# Revit family: Haworth_ASeries_Credenza_1HighStorageEnd
name_source: partatom
category: Furniture Systems
revit_build: Autodesk Revit 2018 (Build: 20170223_1515(x64)
units: mm (PartAtom-declared; Revit-internal decimal feet)

## family parameters
Always vertical = Yes
Cut with Voids When Loaded = No
OmniClass Number = 23.40.70.14.64.21
OmniClass Title = Systems Furniture
Part Type = Normal
Room Calculation Point = No
Round Connector Dimension = Use Diameter
Shared = No
Work Plane-Based = No

## types (9) — shared parameters
Actual Depth = 18"
Actual Height = 21 1/4"
Assembly Code = E2020200
Base Height = 2 1/2"
Classic Pull = Yes
Crescent Pull = No
Custom Size = No
Description = Haworth - ASeries Credenza - 1-High - Storage End
Door Height = 18"
Door Offset = 2"
Drawer Height = 6"
Drawer Height Bottom = 11 15/16"
Ellipse Pull = No
End Shelf Height = 11 1/2"
Front Finish = Haworth _ Laminate _ Linen H-WL
Full Back = Yes
J Pull = No
Linear Pull = No
Manufacturer = Haworth
Max. Height = 21 1/4"
Max. Width = 72"
Metal Offset = 1/16"
Min. Height = 21 1/4"
Min. Width = 48"
Min/Max Widths = 48-72 in.
Model = GCLS
Pull Finish = Haworth _ Metal _ Brushed Aluminum
Radius Pull = No
Revision Number = 2
Shelf Finish = Haworth _ Laminate _ Linen H-WL
Size = Verify Final Dim. w/ Haworth
Standard Base = Yes
Storage Back = No
Sustainability Info = https://www.haworth.com
Taper Pull = No
Toe Kick Base = No
Toe Kick Height = 1 3/4"
Top Finish = Haworth _ Laminate _ Linen H-WL
URL = www.haworth.com
URL - Product = https://www.haworth.com
Warranty = http://www.haworth.com

## per-type parameters (varying)
- 72w - 36w Drawers: Actual Storage Width=36"; Actual Width=72"; Door Center=19 3/8"; Door Width=17 15/16"; Drawers=Yes; Hinged Doors=No; Max. Storage Width=42"; Middle Shelf Height=11 1/2"; Min. Storage Width=30"; Open=No; Panel Center Offset=18 1/8"; Right Panel=Yes; Right Shelf Length=23 7/8"; Shelf Offset=3/4"; Standard Size Doors 48=No; Standard Size Doors 60=No; Standard Size Doors 72=No; Standard Size Lat 48=No; Standard Size Lat 60=No; Standard Size Lat 72=Yes; Standard Size Open 48=No; Standard Size Open 60=No; Standard Size Open 72=No; Storage Width=36"; Width=72"
- 72w - 36w Doors: Actual Storage Width=36"; Actual Width=72"; Door Center=19 3/8"; Door Width=17 15/16"; Drawers=No; Hinged Doors=Yes; Max. Storage Width=42"; Middle Shelf Height=16 3/4"; Min. Storage Width=30"; Open=No; Panel Center Offset=18 1/8"; Right Panel=Yes; Right Shelf Length=23 7/8"; Shelf Offset=3/4"; Standard Size Doors 48=No; Standard Size Doors 60=No; Standard Size Doors 72=Yes; Standard Size Lat 48=No; Standard Size Lat 60=No; Standard Size Lat 72=No; Standard Size Open 48=No; Standard Size Open 60=No; Standard Size Open 72=No; Storage Width=36"; Width=72"
- 72w - 36w Open: Actual Storage Width=36"; Actual Width=72"; Door Center=19 3/8"; Door Width=17 15/16"; Drawers=No; Hinged Doors=No; Max. Storage Width=42"; Middle Shelf Height=11 1/2"; Min. Storage Width=30"; Open=Yes; Panel Center Offset=18 1/8"; Right Panel=Yes; Right Shelf Length=23 7/8"; Shelf Offset=3/4"; Standard Size Doors 48=No; Standard Size Doors 60=No; Standard Size Doors 72=No; Standard Size Lat 48=No; Standard Size Lat 60=No; Standard Size Lat 72=No; Standard Size Open 48=No; Standard Size Open 60=No; Standard Size Open 72=Yes; Storage Width=36"; Width=72"
- 60w - 30w Drawers: Actual Storage Width=30"; Actual Width=60"; Door Center=16 3/8"; Door Width=14 15/16"; Drawers=Yes; Hinged Doors=No; Max. Storage Width=42"; Middle Shelf Height=11 1/2"; Min. Storage Width=30"; Open=No; Panel Center Offset=15 1/8"; Right Panel=Yes; Right Shelf Length=17 7/8"; Shelf Offset=3/4"; Standard Size Doors 48=No; Standard Size Doors 60=No; Standard Size Doors 72=No; Standard Size Lat 48=No; Standard Size Lat 60=Yes; Standard Size Lat 72=No; Standard Size Open 48=No; Standard Size Open 60=No; Standard Size Open 72=No; Storage Width=30"; Width=60"
- 60w - 30w Doors: Actual Storage Width=30"; Actual Width=60"; Door Center=16 3/8"; Door Width=14 15/16"; Drawers=No; Hinged Doors=Yes; Max. Storage Width=42"; Middle Shelf Height=16 3/4"; Min. Storage Width=30"; Open=No; Panel Center Offset=15 1/8"; Right Panel=Yes; Right Shelf Length=17 7/8"; Shelf Offset=3/4"; Standard Size Doors 48=No; Standard Size Doors 60=Yes; Standard Size Doors 72=No; Standard Size Lat 48=No; Standard Size Lat 60=No; Standard Size Lat 72=No; Standard Size Open 48=No; Standard Size Open 60=No; Standard Size Open 72=No; Storage Width=30"; Width=60"
- 60w - 30w Open: Actual Storage Width=30"; Actual Width=60"; Door Center=16 3/8"; Door Width=14 15/16"; Drawers=No; Hinged Doors=No; Max. Storage Width=42"; Middle Shelf Height=11 1/2"; Min. Storage Width=30"; Open=Yes; Panel Center Offset=15 1/8"; Right Panel=Yes; Right Shelf Length=17 7/8"; Shelf Offset=3/4"; Standard Size Doors 48=No; Standard Size Doors 60=No; Standard Size Doors 72=No; Standard Size Lat 48=No; Standard Size Lat 60=No; Standard Size Lat 72=No; Standard Size Open 48=No; Standard Size Open 60=Yes; Standard Size Open 72=No; Storage Width=30"; Width=60"
- 48w - 24w Drawers: Actual Storage Width=24"; Actual Width=48"; Door Center=13 3/8"; Door Width=11 15/16"; Drawers=Yes; Hinged Doors=No; Max. Storage Width=30"; Middle Shelf Height=11 1/2"; Min. Storage Width=24"; Open=No; Panel Center Offset=12 1/8"; Right Panel=No; Right Shelf Length=11 7/8"; Shelf Offset=1/16"; Standard Size Doors 48=No; Standard Size Doors 60=No; Standard Size Doors 72=No; Standard Size Lat 48=Yes; Standard Size Lat 60=No; Standard Size Lat 72=No; Standard Size Open 48=No; Standard Size Open 60=No; Standard Size Open 72=No; Storage Width=24"; Width=48"
- 48w - 24w Doors: Actual Storage Width=24"; Actual Width=48"; Door Center=13 3/8"; Door Width=11 15/16"; Drawers=No; Hinged Doors=Yes; Max. Storage Width=30"; Middle Shelf Height=16 3/4"; Min. Storage Width=24"; Open=No; Panel Center Offset=12 1/8"; Right Panel=No; Right Shelf Length=11 7/8"; Shelf Offset=1/16"; Standard Size Doors 48=Yes; Standard Size Doors 60=No; Standard Size Doors 72=No; Standard Size Lat 48=No; Standard Size Lat 60=No; Standard Size Lat 72=No; Standard Size Open 48=No; Standard Size Open 60=No; Standard Size Open 72=No; Storage Width=24"; Width=48"
- 48w - 24w Open: Actual Storage Width=24"; Actual Width=48"; Door Center=13 3/8"; Door Width=11 15/16"; Drawers=No; Hinged Doors=No; Max. Storage Width=30"; Middle Shelf Height=11 1/2"; Min. Storage Width=24"; Open=Yes; Panel Center Offset=12 1/8"; Right Panel=No; Right Shelf Length=11 7/8"; Shelf Offset=1/16"; Standard Size Doors 48=No; Standard Size Doors 60=No; Standard Size Doors 72=No; Standard Size Lat 48=No; Standard Size Lat 60=No; Standard Size Lat 72=No; Standard Size Open 48=Yes; Standard Size Open 60=No; Standard Size Open 72=No; Storage Width=24"; Width=48"

## geometry (parser evidence)
native form markers: Sweep x11
no freeform markers — native parametric forms only
